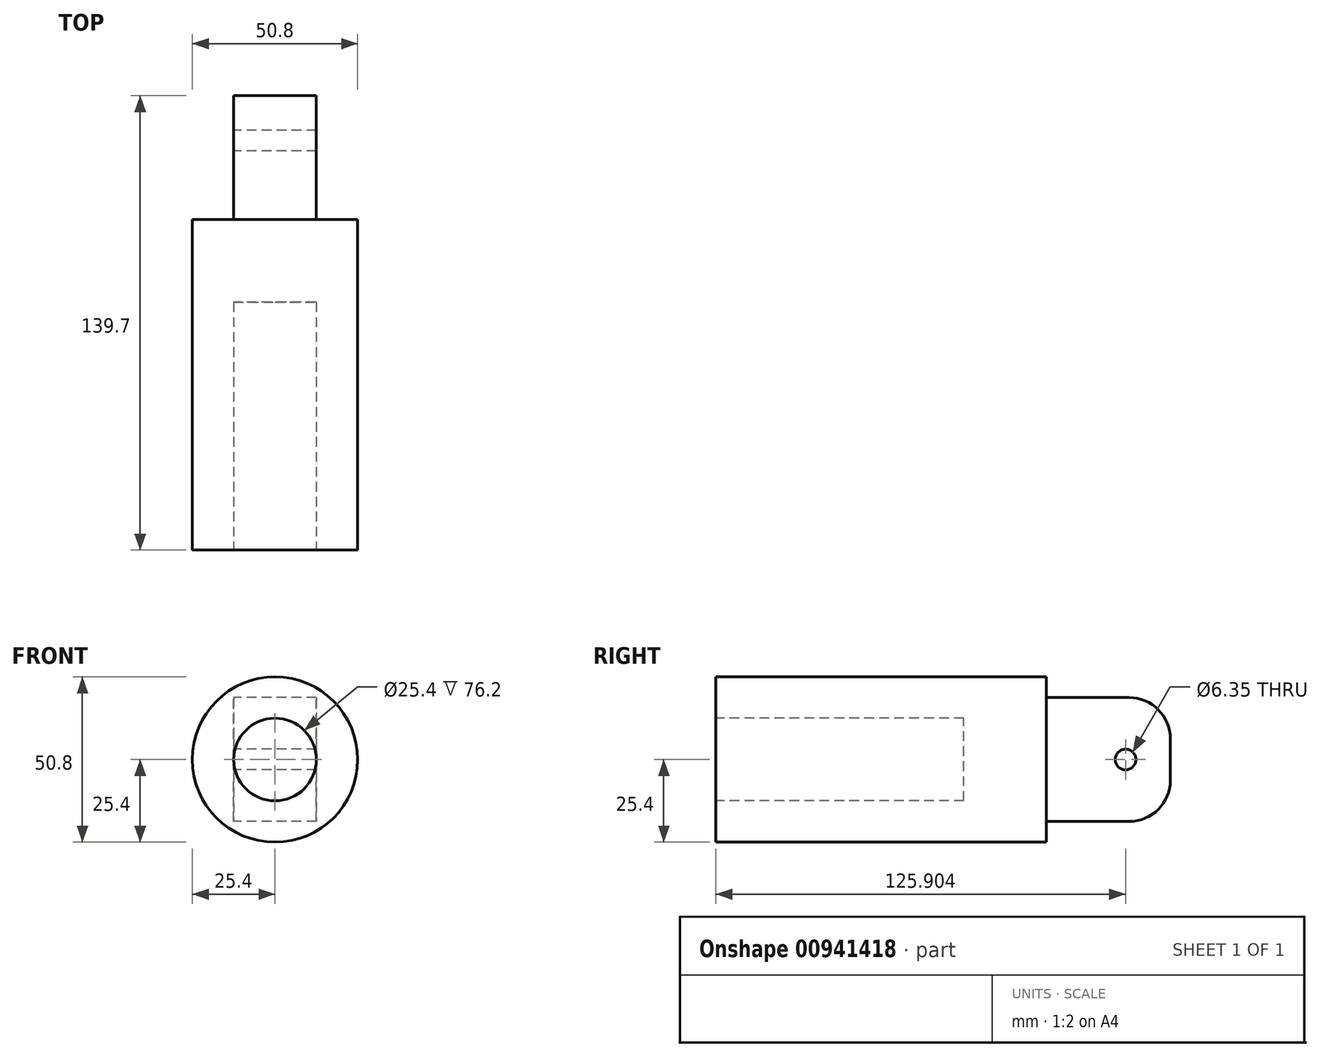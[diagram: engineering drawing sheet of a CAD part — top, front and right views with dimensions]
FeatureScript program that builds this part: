
annotation { "Feature Type Name" : "Feature", "Feature Type Description" : "" }
export const myFeature = defineFeature(function(context is Context, id is Id, definition is map)
    precondition{}
    {
        {
            var Q0;
            Q0=qCreatedBy(makeId("Front.planeOp"),FACE);
            var sketch = newSketch(context, id + "F0", { "sketchPlane" : qUnion([Q0])});
            skCircle(sketch, "E0", {"center": v(0, 0) * mm, "radius": 25.4 * mm});
            skSolve(sketch);
        }
        {
            var Q0;
            Q0=makeQuery(id+"F0.imprint","IMPRINT",FACE,{"disambiguationData":[TD([[makeQuery(id+"F0.imprint","IMPRINT",EDGE,{"derivedFrom":sQuery(id+"F0.wireOp",EDGE,"E0")}),1.0]])]});
            extrude(context, id + "F1", {"entities" : qUnion([Q0]), "depth" : 101.6 * mm, "offsetDistance" : 25.4 * mm});
        }
        {
            var Q0;
            Q0=makeQuery(id+"F1.opExtrude","CAP_FACE",FACE,{"disambiguationData":[OSD([sQuery(id+"F0.wireOp",EDGE,"E0")])],"isStart":false});
            var sketch = newSketch(context, id + "F2", { "sketchPlane" : qUnion([Q0])});
            skCircle(sketch, "E1", {"center": v(0, 0) * mm, "radius": 12.7 * mm});
            skSolve(sketch);
        }
        {
            var Q0;
            Q0=makeQuery(id+"F2.imprint","IMPRINT",FACE,{"disambiguationData":[TD([[makeQuery(id+"F2.imprint","IMPRINT",EDGE,{"derivedFrom":sQuery(id+"F2.wireOp",EDGE,"E1")}),1.0]])]});
            extrude(context, id + "F3", {"entities" : qUnion([Q0]), "operationType" : NewBodyOperationType.REMOVE, "oppositeDirection" : true, "depth" : 76.2 * mm, "offsetDistance" : 25.4 * mm});
        }
        {
            var Q0;
            Q0=qCreatedBy(makeId("Right.planeOp"),FACE);
            var sketch = newSketch(context, id + "F4", { "sketchPlane" : qUnion([Q0])});
            skLineSegment(sketch, "E2.bottom", {"start": v(0, 19.05) * mm, "end": v(38.1, 19.05) * mm});
            skLineSegment(sketch, "E2.top", {"start": v(0, -19.05) * mm, "end": v(38.1, -19.05) * mm});
            skLineSegment(sketch, "E2.left", {"start": v(0, 19.05) * mm, "end": v(0, -19.05) * mm});
            skLineSegment(sketch, "E2.right", {"start": v(38.1, 19.05) * mm, "end": v(38.1, -19.05) * mm});
            skCircle(sketch, "E3", {"center": v(24.3, 0) * mm, "radius": 3.18 * mm});
            skSolve(sketch);
        }
        {
            var Q0;
            Q0=makeQuery(id+"F4.imprint","IMPRINT",FACE,{"disambiguationData":[TD([[makeQuery(id+"F4.imprint","IMPRINT",EDGE,{"derivedFrom":sQuery(id+"F4.wireOp",EDGE,"E2.bottom")}),-1.0]])]});
            extrude(context, id + "F5", {"entities" : qUnion([Q0]), "operationType" : NewBodyOperationType.ADD, "depth" : 25.4 * mm, "offsetDistance" : 25.4 * mm, "symmetric" : true});
        }
        {
            var Q0;
            Q0=makeQuery(id+"F5.opExtrude","SWEPT_EDGE",EDGE,{"disambiguationData":[OSD([sQuery(id+"F4.wireOp",EDGE,"E2.bottom"),sQuery(id+"F4.wireOp",EDGE,"E2.right")])]});
            var Q1;
            Q1=makeQuery(id+"F5.opExtrude","SWEPT_EDGE",EDGE,{"disambiguationData":[OSD([sQuery(id+"F4.wireOp",EDGE,"E2.top"),sQuery(id+"F4.wireOp",EDGE,"E2.right")])]});
            fillet(context, id + "F6", {"entities" : qUnion([Q0, Q1]), "radius" : 12.7 * mm, "tangentPropagation" : true, "allowEdgeOverflow" : false});
        }
    });
